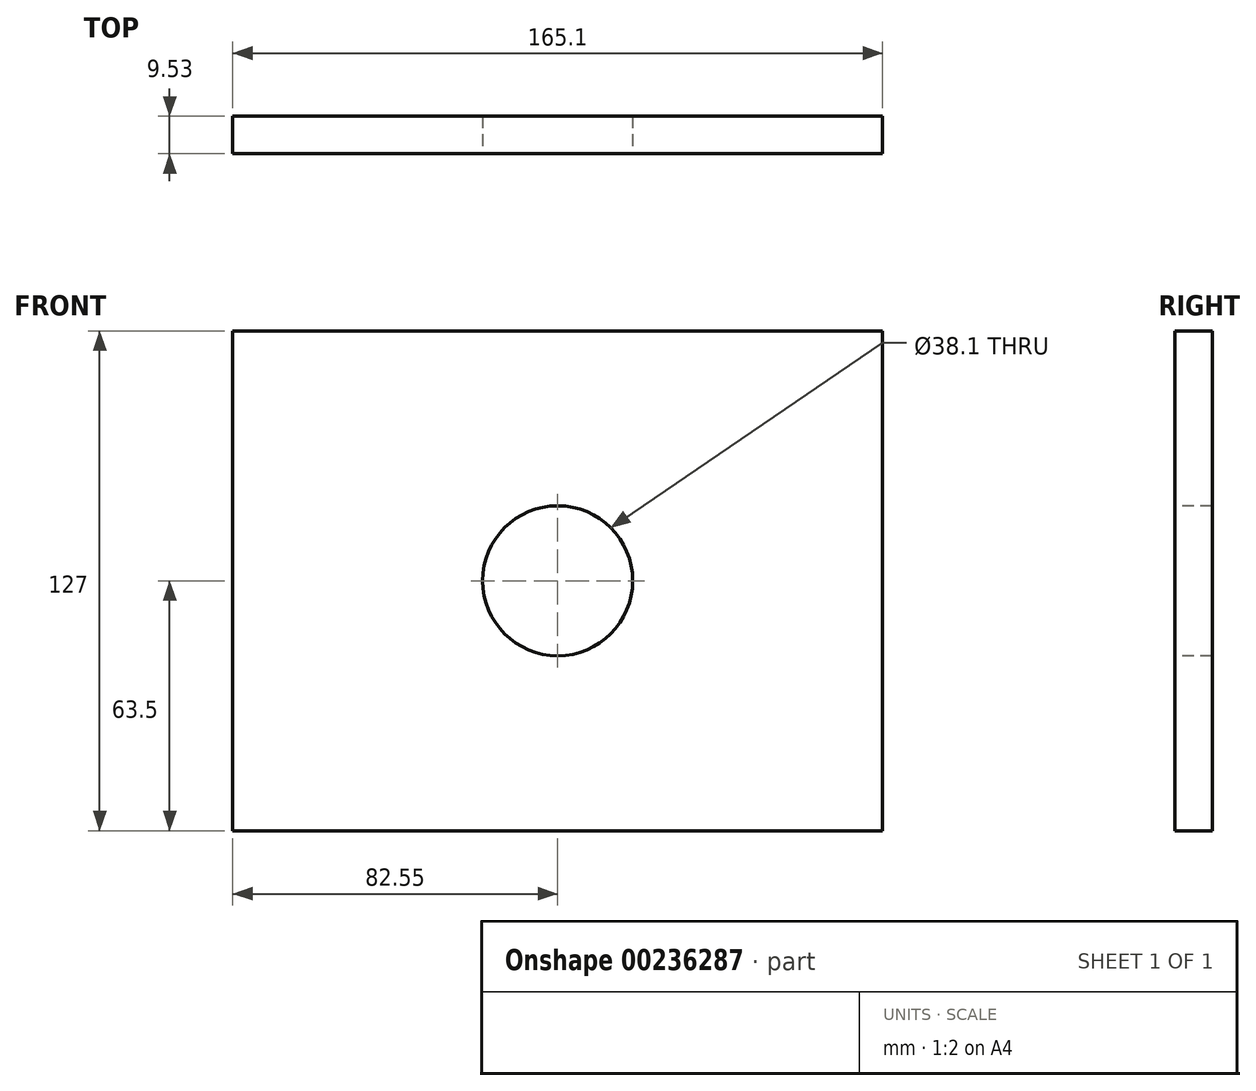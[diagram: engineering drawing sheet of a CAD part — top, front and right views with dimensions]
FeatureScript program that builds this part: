
annotation { "Feature Type Name" : "Feature", "Feature Type Description" : "" }
export const myFeature = defineFeature(function(context is Context, id is Id, definition is map)
    precondition{}
    {
        {
            var Q0;
            Q0=qCreatedBy(makeId("Front.planeOp"),FACE);
            var sketch = newSketch(context, id + "F0", { "sketchPlane" : qUnion([Q0])});
            skLineSegment(sketch, "E0.bottom", {"start": v(82.55, 63.5) * mm, "end": v(-82.55, 63.5) * mm});
            skLineSegment(sketch, "E0.top", {"start": v(82.55, -63.5) * mm, "end": v(-82.55, -63.5) * mm});
            skLineSegment(sketch, "E0.left", {"start": v(82.55, 63.5) * mm, "end": v(82.55, -63.5) * mm});
            skLineSegment(sketch, "E0.right", {"start": v(-82.55, 63.5) * mm, "end": v(-82.55, -63.5) * mm});
            skPoint(sketch, "E0.middle", {"position": v(0, 0) * mm});
            skSolve(sketch);
        }
        {
            var Q0;
            Q0=makeQuery(id+"F0.imprint","IMPRINT",FACE,{"disambiguationData":[TD([[makeQuery(id+"F0.imprint","IMPRINT",EDGE,{"derivedFrom":sQuery(id+"F0.wireOp",EDGE,"E0.bottom")}),1.0]])]});
            extrude(context, id + "F1", {"entities" : qUnion([Q0]), "depth" : 9.52 * mm});
        }
        {
            var Q0;
            Q0=makeQuery(id+"F1.opExtrude","CAP_FACE",FACE,{"disambiguationData":[OSD([sQuery(id+"F0.wireOp",EDGE,"E0.bottom"),sQuery(id+"F0.wireOp",EDGE,"E0.top"),sQuery(id+"F0.wireOp",EDGE,"E0.left"),sQuery(id+"F0.wireOp",EDGE,"E0.right")])],"isStart":false});
            var sketch = newSketch(context, id + "F2", { "sketchPlane" : qUnion([Q0])});
            skCircle(sketch, "E1", {"center": v(0, 0) * mm, "radius": 19.05 * mm});
            skSolve(sketch);
        }
        {
            var Q0;
            Q0 = qSketchRegion(id + "F2", true);
            extrude(context, id + "F3", {"entities" : qUnion([Q0]), "operationType" : NewBodyOperationType.REMOVE, "endBound" : BoundingType.THROUGH_ALL, "oppositeDirection" : true, "depth" : 25.4 * mm});
        }
    });
